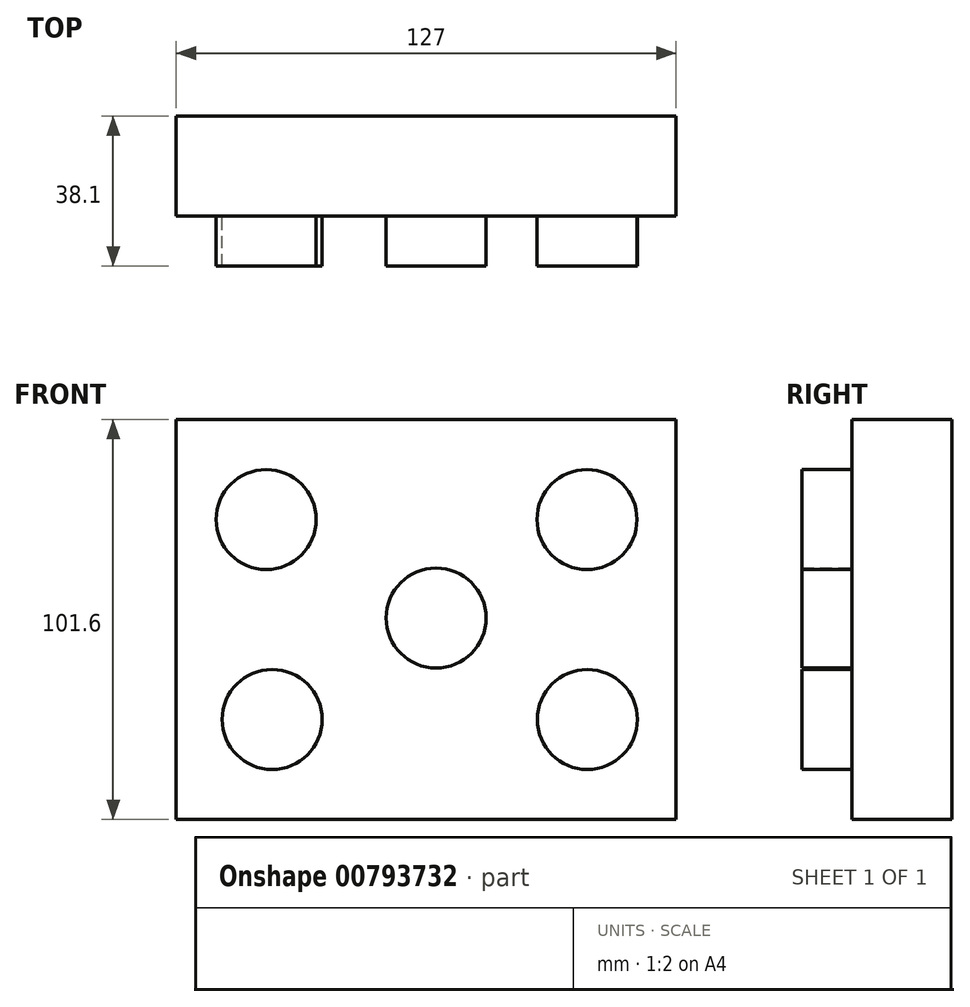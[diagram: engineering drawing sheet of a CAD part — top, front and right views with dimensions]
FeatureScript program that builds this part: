
annotation { "Feature Type Name" : "Feature", "Feature Type Description" : "" }
export const myFeature = defineFeature(function(context is Context, id is Id, definition is map)
    precondition{}
    {
        {
            var Q0;
            Q0=qCreatedBy(makeId("Front.planeOp"),FACE);
            var sketch = newSketch(context, id + "F0", { "sketchPlane" : qUnion([Q0])});
            skLineSegment(sketch, "E0.bottom", {"start": v(-66.04, 50.43) * mm, "end": v(60.96, 50.43) * mm});
            skLineSegment(sketch, "E0.top", {"start": v(-66.04, -51.17) * mm, "end": v(60.96, -51.17) * mm});
            skLineSegment(sketch, "E0.left", {"start": v(-66.04, 50.43) * mm, "end": v(-66.04, -51.17) * mm});
            skLineSegment(sketch, "E0.right", {"start": v(60.96, 50.43) * mm, "end": v(60.96, -51.17) * mm});
            skCircle(sketch, "E1", {"center": v(-43.17, 25.03) * mm, "radius": 12.7 * mm});
            skCircle(sketch, "E2", {"center": v(0, 0) * mm, "radius": 12.7 * mm});
            skCircle(sketch, "E3", {"center": v(38.33, 25.03) * mm, "radius": 12.7 * mm});
            skCircle(sketch, "E4", {"center": v(-41.66, -25.77) * mm, "radius": 12.7 * mm});
            skCircle(sketch, "E5", {"center": v(38.4, -25.77) * mm, "radius": 12.7 * mm});
            skSolve(sketch);
        }
        {
            var Q0;
            Q0=makeQuery(id+"F0.imprint","IMPRINT",FACE,{"disambiguationData":[TD([[makeQuery(id+"F0.imprint","IMPRINT",EDGE,{"derivedFrom":sQuery(id+"F0.wireOp",EDGE,"E0.bottom")}),-1.0]])]});
            extrude(context, id + "F1", {"entities" : qUnion([Q0]), "depth" : 25.4 * mm, "offsetDistance" : 25.4 * mm});
        }
        {
            var Q0;
            Q0=makeQuery(id+"F0.imprint","IMPRINT",FACE,{"disambiguationData":[TD([[makeQuery(id+"F0.imprint","IMPRINT",EDGE,{"derivedFrom":sQuery(id+"F0.wireOp",EDGE,"E1")}),1.0]])]});
            var Q1;
            Q1=makeQuery(id+"F0.imprint","IMPRINT",FACE,{"disambiguationData":[TD([[makeQuery(id+"F0.imprint","IMPRINT",EDGE,{"derivedFrom":sQuery(id+"F0.wireOp",EDGE,"E4")}),1.0]])]});
            var Q2;
            Q2=makeQuery(id+"F0.imprint","IMPRINT",FACE,{"disambiguationData":[TD([[makeQuery(id+"F0.imprint","IMPRINT",EDGE,{"derivedFrom":sQuery(id+"F0.wireOp",EDGE,"E2")}),1.0]])]});
            var Q3;
            Q3=makeQuery(id+"F0.imprint","IMPRINT",FACE,{"disambiguationData":[TD([[makeQuery(id+"F0.imprint","IMPRINT",EDGE,{"derivedFrom":sQuery(id+"F0.wireOp",EDGE,"E3")}),1.0]])]});
            var Q4;
            Q4=makeQuery(id+"F0.imprint","IMPRINT",FACE,{"disambiguationData":[TD([[makeQuery(id+"F0.imprint","IMPRINT",EDGE,{"derivedFrom":sQuery(id+"F0.wireOp",EDGE,"E5")}),1.0]])]});
            extrude(context, id + "F2", {"entities" : qUnion([Q0, Q1, Q2, Q3, Q4]), "operationType" : NewBodyOperationType.ADD, "depth" : 38.1 * mm, "offsetDistance" : 25.4 * mm});
        }
    });
